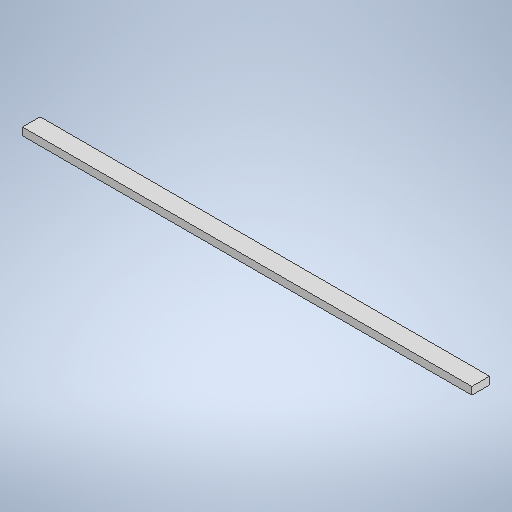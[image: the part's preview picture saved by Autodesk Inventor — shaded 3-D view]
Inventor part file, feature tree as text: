
AUTODESK INVENTOR PART (.ipt)
format: ipt  version: 2025 (Build 290162000, 162)  size: 245,248 bytes
history: native  units: in
note: dims shown in document units (in); Inventor stores cm internally (conversion verified against a paired STEP export)
features: extrude x1, sketch x1
ambient origin geometry x8: Origin, YZ Plane, XZ Plane, XY Plane, X Axis, Y Axis, Z Axis, Center Point
bodies: Solid1 (feature_tree)
feature tree (2):
  extrude  "Extrusion1"  Depth=3.5in
  sketch  "Sketch1"  dims[d0=89.0in d1=3.5in d2=1.5in d3=0.0in]
